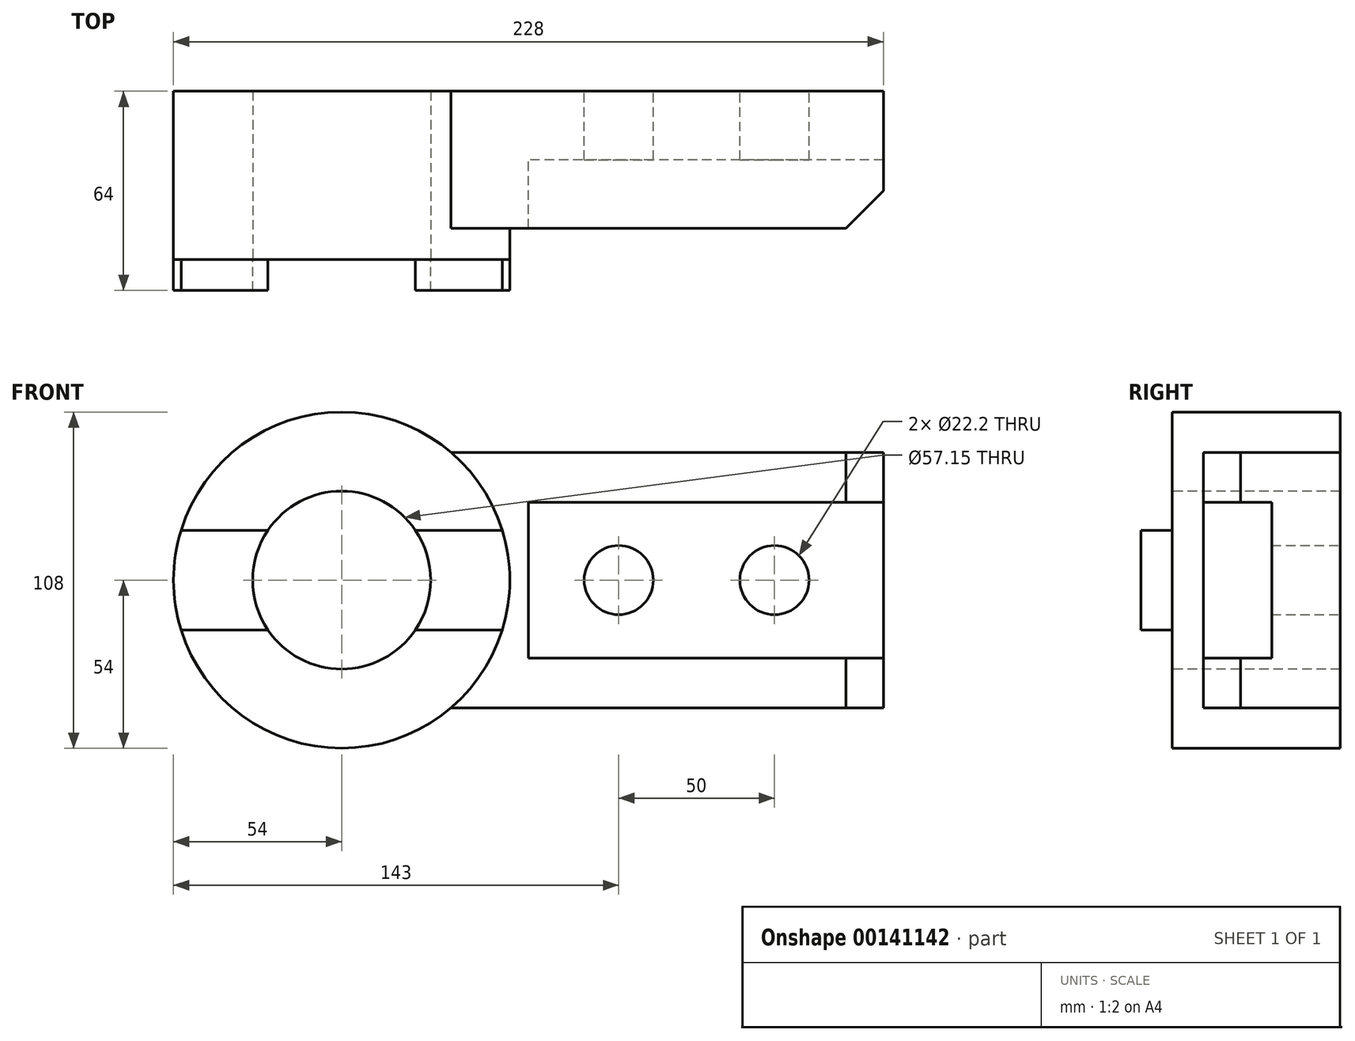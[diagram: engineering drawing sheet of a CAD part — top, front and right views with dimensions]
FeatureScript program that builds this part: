
annotation { "Feature Type Name" : "Feature", "Feature Type Description" : "" }
export const myFeature = defineFeature(function(context is Context, id is Id, definition is map)
    precondition{}
    {
        {
            var Q0;
            Q0=qCreatedBy(makeId("Front.planeOp"),FACE);
            var sketch = newSketch(context, id + "F0", { "sketchPlane" : qUnion([Q0])});
            skCircle(sketch, "E0", {"center": v(0, 0) * mm, "radius": 28.57 * mm});
            skCircle(sketch, "E1", {"center": v(0, 0) * mm, "radius": 54 * mm});
            skLineSegment(sketch, "E2", {"start": v(-23.68, 16) * mm, "end": v(-51.58, 16) * mm});
            skLineSegment(sketch, "E3", {"start": v(-23.68, -16) * mm, "end": v(-51.58, -16) * mm});
            skLineSegment(sketch, "E4.MirrorCS", {"start": v(23.68, 16) * mm, "end": v(51.58, 16) * mm});
            skLineSegment(sketch, "E5.MirrorCS", {"start": v(23.68, -16) * mm, "end": v(51.58, -16) * mm});
            skSolve(sketch);
        }
        {
            var Q0;
            {var subQ0=sQuery(id+"F0.wireOp",EDGE,"E2");Q0=makeQuery(id+"F0.imprint","IMPRINT",FACE,{"disambiguationData":[TD([[makeQuery(id+"F0.imprint","IMPRINT",EDGE,{"derivedFrom":subQ0}),1.0]])]});}
            var Q1;
            {var subQ0=sQuery(id+"F0.wireOp",EDGE,"E4.MirrorCS");Q1=makeQuery(id+"F0.imprint","IMPRINT",FACE,{"disambiguationData":[TD([[makeQuery(id+"F0.imprint","IMPRINT",EDGE,{"derivedFrom":subQ0}),-1.0]])]});}
            extrude(context, id + "F1", {"entities" : qUnion([Q0, Q1]), "depth" : 10 * mm});
        }
        {
            var Q0;
            {var subQ0=sQuery(id+"F0.wireOp",EDGE,"E3");Q0=makeQuery(id+"F0.imprint","IMPRINT",FACE,{"disambiguationData":[TD([[makeQuery(id+"F0.imprint","IMPRINT",EDGE,{"derivedFrom":subQ0}),1.0]])]});}
            var Q1;
            {var subQ0=sQuery(id+"F0.wireOp",EDGE,"E2");Q1=makeQuery(id+"F0.imprint","IMPRINT",FACE,{"disambiguationData":[TD([[makeQuery(id+"F0.imprint","IMPRINT",EDGE,{"derivedFrom":subQ0}),1.0]])]});}
            var Q2;
            {var subQ0=sQuery(id+"F0.wireOp",EDGE,"E4.MirrorCS");Q2=makeQuery(id+"F0.imprint","IMPRINT",FACE,{"disambiguationData":[TD([[makeQuery(id+"F0.imprint","IMPRINT",EDGE,{"derivedFrom":subQ0}),-1.0]])]});}
            var Q3;
            {var subQ0=sQuery(id+"F0.wireOp",EDGE,"E2");Q3=makeQuery(id+"F0.imprint","IMPRINT",FACE,{"disambiguationData":[TD([[makeQuery(id+"F0.imprint","IMPRINT",EDGE,{"derivedFrom":subQ0}),-1.0]])]});}
            extrude(context, id + "F2", {"entities" : qUnion([Q0, Q1, Q2, Q3]), "oppositeDirection" : true, "depth" : 54 * mm});
        }
        {
            var Q0;
            Q0=makeQuery(id+"F2.opExtrude","CAP_FACE",FACE,{"disambiguationData":[OSD([sQuery(id+"F0.wireOp",EDGE,"E0"),sQuery(id+"F0.wireOp",EDGE,"E1")])],"isStart":false});
            var sketch = newSketch(context, id + "F3", { "sketchPlane" : qUnion([Q0])});
            skLineSegment(sketch, "E6", {"start": v(-35.14, 41) * mm, "end": v(-174, 41) * mm});
            skLineSegment(sketch, "E7", {"start": v(-174, 41) * mm, "end": v(-174, -41) * mm});
            skLineSegment(sketch, "E8", {"start": v(-174, -41) * mm, "end": v(-35.14, -41) * mm});
            skLineSegment(sketch, "E9", {"start": v(-174, 25) * mm, "end": v(-60, 25) * mm});
            skLineSegment(sketch, "E10", {"start": v(-60, 25) * mm, "end": v(-60, -25) * mm});
            skLineSegment(sketch, "E11", {"start": v(-60, -25) * mm, "end": v(-174, -25) * mm});
            skCircle(sketch, "E12", {"center": v(-89, 0) * mm, "radius": 11.1 * mm});
            skCircle(sketch, "E13", {"center": v(-139, 0) * mm, "radius": 11.1 * mm});
            skSolve(sketch);
        }
        {
            var Q0;
            {var subQ0=sQuery(id+"F3.wireOp",EDGE,"E9");Q0=makeQuery(id+"F3.imprint","IMPRINT",FACE,{"disambiguationData":[TD([[makeQuery(id+"F3.imprint","IMPRINT",EDGE,{"derivedFrom":subQ0}),-1.0]])]});}
            extrude(context, id + "F4", {"entities" : qUnion([Q0]), "operationType" : NewBodyOperationType.ADD, "oppositeDirection" : true, "depth" : 22 * mm});
        }
        {
            var Q0;
            {var subQ3=sQuery(id+"F3.wireOp",EDGE,"E6");Q0=makeQuery(id+"F3.imprint","IMPRINT",FACE,{"disambiguationData":[TD([[makeQuery(id+"F3.imprint","IMPRINT",EDGE,{"derivedFrom":subQ3}),1.0]])]});}
            extrude(context, id + "F5", {"entities" : qUnion([Q0]), "operationType" : NewBodyOperationType.ADD, "oppositeDirection" : true, "depth" : 44 * mm});
        }
        {
            var Q0;
            Q0=makeQuery(id+"F5.opExtrude","SWEPT_FACE",FACE,{"disambiguationData":[OSD([sQuery(id+"F3.wireOp",EDGE,"E8")])]});
            var sketch = newSketch(context, id + "F6", { "sketchPlane" : qUnion([Q0])});
            skLineSegment(sketch, "E14", {"start": v(174, -10) * mm, "end": v(162, -10) * mm});
            skLineSegment(sketch, "E15", {"start": v(162, -10) * mm, "end": v(174, -22) * mm});
            skSolve(sketch);
        }
        {
            var Q0;
            {var subQ0=sQuery(id+"F6.wireOp",EDGE,"E14");Q0=makeQuery(id+"F6.imprint","IMPRINT",FACE,{"disambiguationData":[TD([[makeQuery(id+"F6.imprint","IMPRINT",EDGE,{"derivedFrom":subQ0}),1.0]])]});}
            var Q1;
            Q1=makeQuery(id+"F5.opExtrude","SWEPT_FACE",FACE,{"disambiguationData":[OSD([sQuery(id+"F3.wireOp",EDGE,"E6")])]});
            extrude(context, id + "F7", {"entities" : qUnion([Q0]), "operationType" : NewBodyOperationType.REMOVE, "endBound" : BoundingType.UP_TO_SURFACE, "oppositeDirection" : true, "endBoundEntityFace" : qUnion([Q1]), "depth" : 25 * mm});
        }
    });
